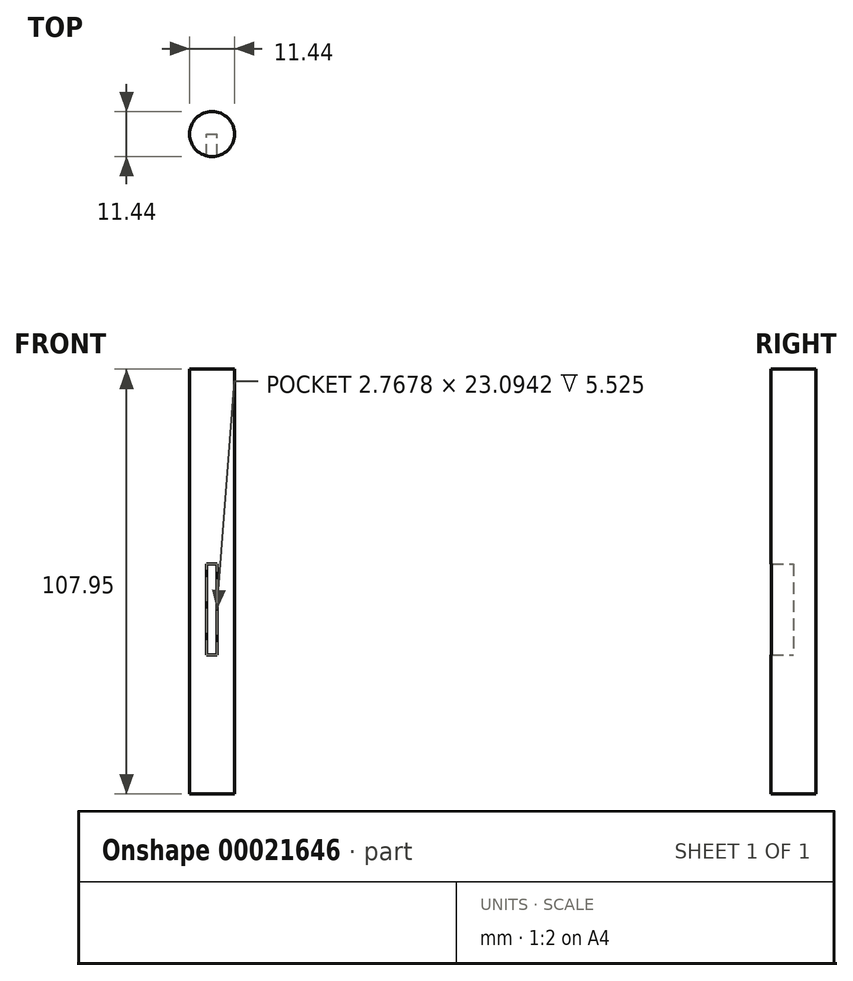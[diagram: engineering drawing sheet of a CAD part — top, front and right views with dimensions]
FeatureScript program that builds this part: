
annotation { "Feature Type Name" : "Feature", "Feature Type Description" : "" }
export const myFeature = defineFeature(function(context is Context, id is Id, definition is map)
    precondition{}
    {
        {
            var Q0;
            Q0=qCreatedBy(makeId("Top.planeOp"),FACE);
            var sketch = newSketch(context, id + "F0", { "sketchPlane" : qUnion([Q0])});
            skCircle(sketch, "E0", {"center": v(0, 0) * mm, "radius": 5.72 * mm});
            skSolve(sketch);
        }
        {
            var Q0;
            Q0 = qSketchRegion(id + "F0", true);
            extrude(context, id + "F1", {"entities" : qUnion([Q0]), "depth" : 107.95 * mm});
        }
        {
            var Q0;
            Q0=qCreatedBy(makeId("Front.planeOp"),FACE);
            var sketch = newSketch(context, id + "F2", { "sketchPlane" : qUnion([Q0])});
            skLineSegment(sketch, "E1.bottom", {"start": v(-1.46, 58.4) * mm, "end": v(1.3, 58.4) * mm});
            skLineSegment(sketch, "E1.top", {"start": v(-1.46, 35.3) * mm, "end": v(1.3, 35.3) * mm});
            skLineSegment(sketch, "E1.left", {"start": v(-1.46, 58.4) * mm, "end": v(-1.46, 35.3) * mm});
            skLineSegment(sketch, "E1.right", {"start": v(1.3, 58.4) * mm, "end": v(1.3, 35.3) * mm});
            skSolve(sketch);
        }
        {
            var Q0;
            Q0 = qSketchRegion(id + "F2", true);
            extrude(context, id + "F3", {"entities" : qUnion([Q0]), "operationType" : NewBodyOperationType.REMOVE, "endBound" : BoundingType.THROUGH_ALL, "depth" : 25.4 * mm});
        }
    });
